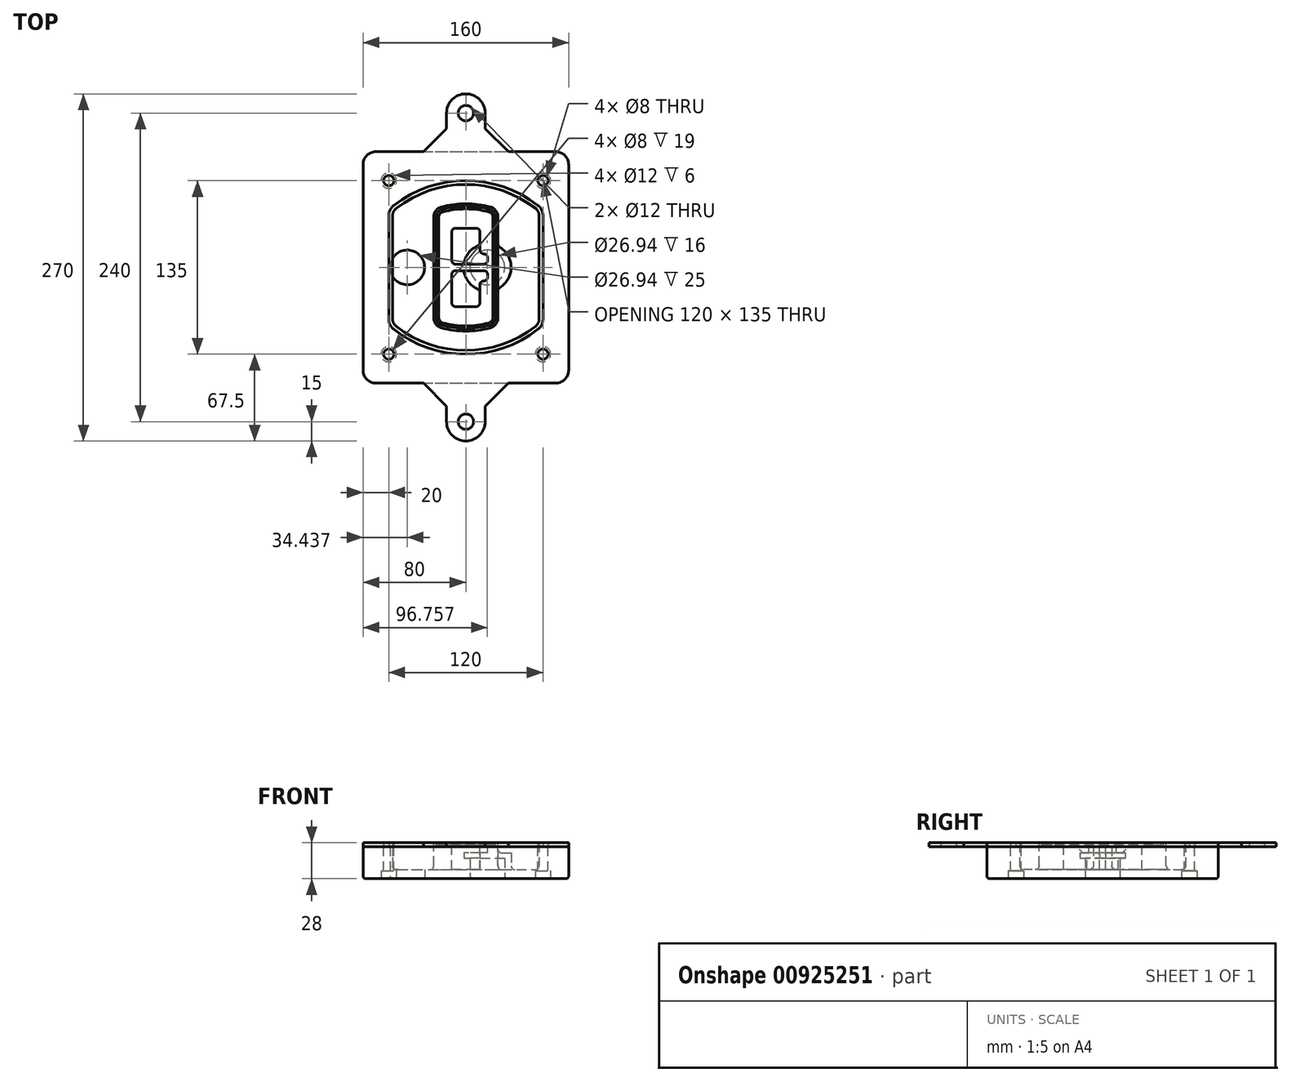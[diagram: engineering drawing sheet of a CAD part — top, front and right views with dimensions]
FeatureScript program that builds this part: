
annotation { "Feature Type Name" : "Feature", "Feature Type Description" : "" }
export const myFeature = defineFeature(function(context is Context, id is Id, definition is map)
    precondition{}
    {
        {
            var Q0;
            Q0=qCreatedBy(makeId("Top.planeOp"),FACE);
            var sketch = newSketch(context, id + "F0", { "sketchPlane" : qUnion([Q0])});
            skPoint(sketch, "E0.rect.middle", {"position": v(0, 0) * mm});
            skLineSegment(sketch, "E1.bottom", {"start": v(-70, -90) * mm, "end": v(70, -90) * mm});
            skLineSegment(sketch, "E1.top", {"start": v(-70, 90) * mm, "end": v(70, 90) * mm});
            skLineSegment(sketch, "E1.left", {"start": v(-80, -80) * mm, "end": v(-80, 80) * mm});
            skLineSegment(sketch, "E1.right", {"start": v(80, -80) * mm, "end": v(80, 80) * mm});
            skLineSegment(sketch, "E2", {"start": v(-80, 90) * mm, "end": v(80, -90) * mm, "construction": true});
            skLineSegment(sketch, "E3", {"start": v(80, 90) * mm, "end": v(-80, -90) * mm, "construction": true});
            skCircle(sketch, "E4", {"center": v(-60, 67.5) * mm, "radius": 4 * mm});
            skCircle(sketch, "E5", {"center": v(60, 67.5) * mm, "radius": 4 * mm});
            skCircle(sketch, "E6", {"center": v(60, -67.5) * mm, "radius": 4 * mm});
            skCircle(sketch, "E7", {"center": v(-60, -67.5) * mm, "radius": 4 * mm});
            skLineSegment(sketch, "E8", {"start": v(-60, 67.5) * mm, "end": v(60, 67.5) * mm, "construction": true});
            skLineSegment(sketch, "E9", {"start": v(60, 67.5) * mm, "end": v(60, -67.5) * mm, "construction": true});
            skLineSegment(sketch, "E10", {"start": v(60, -67.5) * mm, "end": v(-60, -67.5) * mm, "construction": true});
            skLineSegment(sketch, "E11", {"start": v(-60, -67.5) * mm, "end": v(-60, 67.5) * mm, "construction": true});
            skLineSegment(sketch, "E12", {"start": v(-60, 40.3) * mm, "end": v(-60, -40.3) * mm});
            skLineSegment(sketch, "E13", {"start": v(60, 40.3) * mm, "end": v(60, -40.3) * mm});
            skArc(sketch, "E14", {"start": v(56.15, 48.18) * mm, "mid": v(0, 67.5) * mm, "end": v(-56.15, 48.18) * mm});
            skArc(sketch, "E15", {"start": v(-56.15, -48.18) * mm, "mid": v(0, -67.5) * mm, "end": v(56.15, -48.18) * mm});
            skLineSegment(sketch, "E16", {"start": v(-60, 0) * mm, "end": v(60, 0) * mm, "construction": true});
            skPoint(sketch, "E17.visualSharp", {"position": v(-60, -45) * mm});
            skArc(sketch, "E17.filletArc", {"start": v(-60, -40.3) * mm, "mid": v(-58.99, -44.68) * mm, "end": v(-56.15, -48.18) * mm});
            skPoint(sketch, "E18.visualSharp", {"position": v(-60, 45) * mm});
            skArc(sketch, "E18.filletArc", {"start": v(-56.15, 48.18) * mm, "mid": v(-58.99, 44.68) * mm, "end": v(-60, 40.3) * mm});
            skPoint(sketch, "E19.visualSharp", {"position": v(60, 45) * mm});
            skArc(sketch, "E19.filletArc", {"start": v(60, 40.3) * mm, "mid": v(58.99, 44.68) * mm, "end": v(56.15, 48.18) * mm});
            skPoint(sketch, "E20.visualSharp", {"position": v(60, -45) * mm});
            skArc(sketch, "E20.filletArc", {"start": v(56.15, -48.18) * mm, "mid": v(58.99, -44.68) * mm, "end": v(60, -40.3) * mm});
            skPoint(sketch, "E21.visualSharp", {"position": v(-80, 90) * mm});
            skArc(sketch, "E21.filletArc", {"start": v(-70, 90) * mm, "mid": v(-77.07, 87.07) * mm, "end": v(-80, 80) * mm});
            skPoint(sketch, "E22.visualSharp", {"position": v(80, 90) * mm});
            skArc(sketch, "E22.filletArc", {"start": v(80, 80) * mm, "mid": v(77.07, 87.07) * mm, "end": v(70, 90) * mm});
            skPoint(sketch, "E23.visualSharp", {"position": v(80, -90) * mm});
            skArc(sketch, "E23.filletArc", {"start": v(70, -90) * mm, "mid": v(77.07, -87.07) * mm, "end": v(80, -80) * mm});
            skPoint(sketch, "E24.visualSharp", {"position": v(-80, -90) * mm});
            skArc(sketch, "E24.filletArc", {"start": v(-80, -80) * mm, "mid": v(-77.07, -87.07) * mm, "end": v(-70, -90) * mm});
            skArc(sketch, "E25.0", {"start": v(57, 40.3) * mm, "mid": v(56.3, 43.36) * mm, "end": v(54.3, 45.81) * mm});
            skLineSegment(sketch, "E25.1", {"start": v(57, 40.3) * mm, "end": v(57, -40.3) * mm});
            skArc(sketch, "E25.2", {"start": v(54.3, -45.81) * mm, "mid": v(56.3, -43.36) * mm, "end": v(57, -40.3) * mm});
            skArc(sketch, "E25.3", {"start": v(-54.3, -45.81) * mm, "mid": v(0, -64.5) * mm, "end": v(54.3, -45.81) * mm});
            skArc(sketch, "E25.4", {"start": v(-57, -40.3) * mm, "mid": v(-56.3, -43.36) * mm, "end": v(-54.3, -45.81) * mm});
            skArc(sketch, "E25.5", {"start": v(54.3, 45.81) * mm, "mid": v(0, 64.5) * mm, "end": v(-54.3, 45.81) * mm});
            skLineSegment(sketch, "E25.6", {"start": v(-57, 40.3) * mm, "end": v(-57, -40.3) * mm});
            skArc(sketch, "E25.7", {"start": v(-54.3, 45.81) * mm, "mid": v(-56.3, 43.36) * mm, "end": v(-57, 40.3) * mm});
            skArc(sketch, "E26.0", {"start": v(-58.62, 51.33) * mm, "mid": v(-62.58, 46.43) * mm, "end": v(-64, 40.3) * mm});
            skArc(sketch, "E26.1", {"start": v(58.62, 51.33) * mm, "mid": v(0, 71.5) * mm, "end": v(-58.62, 51.33) * mm});
            skArc(sketch, "E26.2", {"start": v(64, 40.3) * mm, "mid": v(62.58, 46.43) * mm, "end": v(58.62, 51.33) * mm});
            skLineSegment(sketch, "E26.3", {"start": v(64, 40.3) * mm, "end": v(64, -40.3) * mm});
            skArc(sketch, "E26.4", {"start": v(58.62, -51.33) * mm, "mid": v(62.58, -46.43) * mm, "end": v(64, -40.3) * mm});
            skLineSegment(sketch, "E26.5", {"start": v(-64, 40.3) * mm, "end": v(-64, -40.3) * mm});
            skArc(sketch, "E26.6", {"start": v(-58.62, -51.33) * mm, "mid": v(0, -71.5) * mm, "end": v(58.62, -51.33) * mm});
            skArc(sketch, "E26.7", {"start": v(-64, -40.3) * mm, "mid": v(-62.58, -46.43) * mm, "end": v(-58.62, -51.33) * mm});
            skSolve(sketch);
        }
        {
            var Q0;
            Q0=makeQuery(id+"F0.imprint","IMPRINT",FACE,{"disambiguationData":[TD([[makeQuery(id+"F0.imprint","IMPRINT",EDGE,{"derivedFrom":sQuery(id+"F0.wireOp",EDGE,"E1.bottom")}),1.0]])]});
            var Q1;
            Q1=makeQuery(id+"F0.imprint","IMPRINT",FACE,{"disambiguationData":[TD([[makeQuery(id+"F0.imprint","IMPRINT",EDGE,{"derivedFrom":sQuery(id+"F0.wireOp",EDGE,"E12")}),1.0]])]});
            var Q2;
            Q2=makeQuery(id+"F0.imprint","IMPRINT",FACE,{"disambiguationData":[TD([[makeQuery(id+"F0.imprint","IMPRINT",EDGE,{"derivedFrom":sQuery(id+"F0.wireOp",EDGE,"E25.0")}),1.0]])]});
            var Q3;
            Q3=makeQuery(id+"F0.imprint","IMPRINT",FACE,{"disambiguationData":[TD([[makeQuery(id+"F0.imprint","IMPRINT",EDGE,{"derivedFrom":sQuery(id+"F0.wireOp",EDGE,"E12")}),-1.0]])]});
            extrude(context, id + "F1", {"entities" : qUnion([Q0, Q1, Q2, Q3]), "oppositeDirection" : true, "depth" : 25 * mm});
        }
        {
            var Q0;
            Q0=makeQuery(id+"F0.imprint","IMPRINT",FACE,{"disambiguationData":[TD([[makeQuery(id+"F0.imprint","IMPRINT",EDGE,{"derivedFrom":sQuery(id+"F0.wireOp",EDGE,"E12")}),1.0]])]});
            extrude(context, id + "F2", {"entities" : qUnion([Q0]), "operationType" : NewBodyOperationType.ADD, "depth" : 3 * mm});
        }
        {
            var Q0;
            Q0=makeQuery(id+"F0.imprint","IMPRINT",FACE,{"disambiguationData":[TD([[makeQuery(id+"F0.imprint","IMPRINT",EDGE,{"derivedFrom":sQuery(id+"F0.wireOp",EDGE,"E25.0")}),1.0]])]});
            extrude(context, id + "F3", {"entities" : qUnion([Q0]), "operationType" : NewBodyOperationType.REMOVE, "oppositeDirection" : true, "depth" : 18 * mm});
        }
        {
            var Q0;
            Q0=makeQuery(id+"F2.opExtrude","CAP_FACE",FACE,{"disambiguationData":[OSD([sQuery(id+"F0.wireOp",EDGE,"E12"),sQuery(id+"F0.wireOp",EDGE,"E13"),sQuery(id+"F0.wireOp",EDGE,"E14"),sQuery(id+"F0.wireOp",EDGE,"E15"),sQuery(id+"F0.wireOp",EDGE,"E17.filletArc"),sQuery(id+"F0.wireOp",EDGE,"E18.filletArc"),sQuery(id+"F0.wireOp",EDGE,"E19.filletArc"),sQuery(id+"F0.wireOp",EDGE,"E20.filletArc"),sQuery(id+"F0.wireOp",EDGE,"E25.0"),sQuery(id+"F0.wireOp",EDGE,"E25.1"),sQuery(id+"F0.wireOp",EDGE,"E25.2"),sQuery(id+"F0.wireOp",EDGE,"E25.3"),sQuery(id+"F0.wireOp",EDGE,"E25.4"),sQuery(id+"F0.wireOp",EDGE,"E25.5"),sQuery(id+"F0.wireOp",EDGE,"E25.6"),sQuery(id+"F0.wireOp",EDGE,"E25.7")])],"isStart":false});
            var sketch = newSketch(context, id + "F4", { "sketchPlane" : qUnion([Q0])});
            skArc(sketch, "E27.0", {"start": v(-19.08, -46.97) * mm, "mid": v(0, -49.5) * mm, "end": v(19.08, -46.97) * mm});
            skArc(sketch, "E28.0", {"start": v(19.08, 46.97) * mm, "mid": v(0, 49.5) * mm, "end": v(-19.08, 46.97) * mm});
            skLineSegment(sketch, "E29", {"start": v(-25, 39.25) * mm, "end": v(-25, -39.25) * mm});
            skLineSegment(sketch, "E30", {"start": v(25, 39.25) * mm, "end": v(25, -39.25) * mm});
            skLineSegment(sketch, "E31", {"start": v(-25, 45.1) * mm, "end": v(25, 45.1) * mm, "construction": true});
            skLineSegment(sketch, "E32", {"start": v(-25, -45.1) * mm, "end": v(25, -45.1) * mm, "construction": true});
            skPoint(sketch, "E33.visualSharp", {"position": v(-25, 45.1) * mm});
            skArc(sketch, "E33.filletArc", {"start": v(-19.08, 46.97) * mm, "mid": v(-23.35, 44.11) * mm, "end": v(-25, 39.25) * mm});
            skPoint(sketch, "E34.visualSharp", {"position": v(25, 45.1) * mm});
            skArc(sketch, "E34.filletArc", {"start": v(25, 39.25) * mm, "mid": v(23.35, 44.11) * mm, "end": v(19.08, 46.97) * mm});
            skPoint(sketch, "E35.visualSharp", {"position": v(25, -45.1) * mm});
            skArc(sketch, "E35.filletArc", {"start": v(19.08, -46.97) * mm, "mid": v(23.35, -44.11) * mm, "end": v(25, -39.25) * mm});
            skPoint(sketch, "E36.visualSharp", {"position": v(-25, -45.1) * mm});
            skArc(sketch, "E36.filletArc", {"start": v(-25, -39.25) * mm, "mid": v(-23.35, -44.11) * mm, "end": v(-19.08, -46.97) * mm});
            skArc(sketch, "E37.0", {"start": v(54.3, 45.81) * mm, "mid": v(0, 64.5) * mm, "end": v(-54.3, 45.81) * mm});
            skArc(sketch, "E37.1", {"start": v(-54.3, 45.81) * mm, "mid": v(-56.3, 43.36) * mm, "end": v(-57, 40.3) * mm});
            skLineSegment(sketch, "E37.2", {"start": v(-57, 40.3) * mm, "end": v(-57, -40.3) * mm});
            skArc(sketch, "E37.3", {"start": v(-57, -40.3) * mm, "mid": v(-56.3, -43.36) * mm, "end": v(-54.3, -45.81) * mm});
            skArc(sketch, "E37.4", {"start": v(-54.3, -45.81) * mm, "mid": v(0, -64.5) * mm, "end": v(54.3, -45.81) * mm});
            skArc(sketch, "E37.5", {"start": v(54.3, -45.81) * mm, "mid": v(56.3, -43.36) * mm, "end": v(57, -40.3) * mm});
            skLineSegment(sketch, "E37.6", {"start": v(57, 40.3) * mm, "end": v(57, -40.3) * mm});
            skArc(sketch, "E37.7", {"start": v(57, 40.3) * mm, "mid": v(56.3, 43.36) * mm, "end": v(54.3, 45.81) * mm});
            skLineSegment(sketch, "E38.0", {"start": v(23, 39.25) * mm, "end": v(23, -39.25) * mm});
            skArc(sketch, "E38.1", {"start": v(18.56, -45.04) * mm, "mid": v(21.76, -42.9) * mm, "end": v(23, -39.25) * mm});
            skArc(sketch, "E38.2", {"start": v(-18.56, -45.04) * mm, "mid": v(0, -47.5) * mm, "end": v(18.56, -45.04) * mm});
            skArc(sketch, "E38.3", {"start": v(-23, -39.25) * mm, "mid": v(-21.76, -42.9) * mm, "end": v(-18.56, -45.04) * mm});
            skLineSegment(sketch, "E38.4", {"start": v(-23, 39.25) * mm, "end": v(-23, -39.25) * mm});
            skArc(sketch, "E38.5", {"start": v(23, 39.25) * mm, "mid": v(21.76, 42.9) * mm, "end": v(18.56, 45.04) * mm});
            skArc(sketch, "E38.6", {"start": v(-18.56, 45.04) * mm, "mid": v(-21.76, 42.9) * mm, "end": v(-23, 39.25) * mm});
            skArc(sketch, "E38.7", {"start": v(18.56, 45.04) * mm, "mid": v(0, 47.5) * mm, "end": v(-18.56, 45.04) * mm});
            skArc(sketch, "E39.0", {"start": v(21, 39.25) * mm, "mid": v(20.18, 41.68) * mm, "end": v(18.04, 43.1) * mm});
            skLineSegment(sketch, "E39.1", {"start": v(21, 39.25) * mm, "end": v(21, -39.25) * mm});
            skArc(sketch, "E39.2", {"start": v(18.04, -43.1) * mm, "mid": v(20.18, -41.68) * mm, "end": v(21, -39.25) * mm});
            skArc(sketch, "E39.3", {"start": v(-18.04, -43.1) * mm, "mid": v(0, -45.5) * mm, "end": v(18.04, -43.1) * mm});
            skArc(sketch, "E39.4", {"start": v(-21, -39.25) * mm, "mid": v(-20.18, -41.68) * mm, "end": v(-18.04, -43.1) * mm});
            skArc(sketch, "E39.5", {"start": v(18.04, 43.1) * mm, "mid": v(0, 45.5) * mm, "end": v(-18.04, 43.1) * mm});
            skLineSegment(sketch, "E39.6", {"start": v(-21, 39.25) * mm, "end": v(-21, -39.25) * mm});
            skArc(sketch, "E39.7", {"start": v(-18.04, 43.1) * mm, "mid": v(-20.18, 41.68) * mm, "end": v(-21, 39.25) * mm});
            skLineSegment(sketch, "E40", {"start": v(-25, 0) * mm, "end": v(25, 0) * mm, "construction": true});
            skLineSegment(sketch, "E41", {"start": v(-11, 5.5) * mm, "end": v(-11, 27.5) * mm});
            skLineSegment(sketch, "E42", {"start": v(-8, 30.5) * mm, "end": v(8, 30.5) * mm});
            skLineSegment(sketch, "E43", {"start": v(11, 27.5) * mm, "end": v(11, 13.5) * mm});
            skLineSegment(sketch, "E44", {"start": v(14, 10.5) * mm, "end": v(14, 10.5) * mm});
            skLineSegment(sketch, "E45", {"start": v(17, 7.5) * mm, "end": v(17, 5.5) * mm});
            skLineSegment(sketch, "E46", {"start": v(14, 2.5) * mm, "end": v(-8, 2.5) * mm});
            skPoint(sketch, "E47.visualSharp", {"position": v(-11, 30.5) * mm});
            skArc(sketch, "E47.filletArc", {"start": v(-8, 30.5) * mm, "mid": v(-10.12, 29.62) * mm, "end": v(-11, 27.5) * mm});
            skPoint(sketch, "E48.visualSharp", {"position": v(11, 30.5) * mm});
            skArc(sketch, "E48.filletArc", {"start": v(11, 27.5) * mm, "mid": v(10.12, 29.62) * mm, "end": v(8, 30.5) * mm});
            skPoint(sketch, "E49.visualSharp", {"position": v(11, 10.5) * mm});
            skArc(sketch, "E49.filletArc", {"start": v(11, 13.5) * mm, "mid": v(11.88, 11.38) * mm, "end": v(14, 10.5) * mm});
            skPoint(sketch, "E50.visualSharp", {"position": v(17, 10.5) * mm});
            skArc(sketch, "E50.filletArc", {"start": v(17, 7.5) * mm, "mid": v(16.12, 9.62) * mm, "end": v(14, 10.5) * mm});
            skPoint(sketch, "E51.visualSharp", {"position": v(17, 2.5) * mm});
            skArc(sketch, "E51.filletArc", {"start": v(14, 2.5) * mm, "mid": v(16.12, 3.38) * mm, "end": v(17, 5.5) * mm});
            skPoint(sketch, "E52.visualSharp", {"position": v(-11, 2.5) * mm});
            skArc(sketch, "E52.filletArc", {"start": v(-11, 5.5) * mm, "mid": v(-10.12, 3.38) * mm, "end": v(-8, 2.5) * mm});
            skLineSegment(sketch, "E53.0.MirrorCS", {"start": v(14, -2.5) * mm, "end": v(-8, -2.5) * mm});
            skArc(sketch, "E54.0.MirrorCS", {"start": v(-11, -5.5) * mm, "mid": v(-10.12, -3.38) * mm, "end": v(-8, -2.5) * mm});
            skLineSegment(sketch, "E55.0.MirrorCS", {"start": v(-11, -5.5) * mm, "end": v(-11, -27.5) * mm});
            skArc(sketch, "E56.0.MirrorCS", {"start": v(-8, -30.5) * mm, "mid": v(-10.12, -29.62) * mm, "end": v(-11, -27.5) * mm});
            skLineSegment(sketch, "E57.0.MirrorCS", {"start": v(-8, -30.5) * mm, "end": v(8, -30.5) * mm});
            skArc(sketch, "E58.0.MirrorCS", {"start": v(11, -27.5) * mm, "mid": v(10.12, -29.62) * mm, "end": v(8, -30.5) * mm});
            skLineSegment(sketch, "E59.0.MirrorCS", {"start": v(11, -27.5) * mm, "end": v(11, -13.5) * mm});
            skArc(sketch, "E60.0.MirrorCS", {"start": v(11, -13.5) * mm, "mid": v(11.88, -11.38) * mm, "end": v(14, -10.5) * mm});
            skArc(sketch, "E61.0.MirrorCS", {"start": v(17, -7.5) * mm, "mid": v(16.12, -9.62) * mm, "end": v(14, -10.5) * mm});
            skLineSegment(sketch, "E62.0.MirrorCS", {"start": v(17, -7.5) * mm, "end": v(17, -5.5) * mm});
            skArc(sketch, "E63.0.MirrorCS", {"start": v(14, -2.5) * mm, "mid": v(16.12, -3.38) * mm, "end": v(17, -5.5) * mm});
            skSolve(sketch);
        }
        {
            var Q0;
            Q0=makeQuery(id+"F4.imprint","IMPRINT",FACE,{"disambiguationData":[TD([[makeQuery(id+"F4.imprint","IMPRINT",EDGE,{"derivedFrom":sQuery(id+"F4.wireOp",EDGE,"E27.0")}),1.0]])]});
            var Q1;
            Q1=makeQuery(id+"F4.imprint","IMPRINT",FACE,{"disambiguationData":[TD([[makeQuery(id+"F4.imprint","IMPRINT",EDGE,{"derivedFrom":sQuery(id+"F4.wireOp",EDGE,"E38.0")}),-1.0]])]});
            var Q2;
            Q2=makeQuery(id+"F4.imprint","IMPRINT",FACE,{"disambiguationData":[TD([[makeQuery(id+"F4.imprint","IMPRINT",EDGE,{"derivedFrom":sQuery(id+"F4.wireOp",EDGE,"E39.0")}),1.0]])]});
            extrude(context, id + "F5", {"entities" : qUnion([Q0, Q1, Q2]), "operationType" : NewBodyOperationType.ADD, "endBound" : BoundingType.UP_TO_NEXT, "oppositeDirection" : true, "depth" : 25 * mm});
        }
        {
            var Q0;
            Q0=makeQuery(id+"F4.imprint","IMPRINT",FACE,{"disambiguationData":[TD([[makeQuery(id+"F4.imprint","IMPRINT",EDGE,{"derivedFrom":sQuery(id+"F4.wireOp",EDGE,"E38.0")}),-1.0]])]});
            extrude(context, id + "F6", {"entities" : qUnion([Q0]), "operationType" : NewBodyOperationType.REMOVE, "oppositeDirection" : true, "depth" : 2 * mm});
        }
        {
            var Q0;
            Q0=makeQuery(id+"F1.opExtrude","CAP_FACE",FACE,{"disambiguationData":[OSD([sQuery(id+"F0.wireOp",EDGE,"E1.bottom"),sQuery(id+"F0.wireOp",EDGE,"E1.top"),sQuery(id+"F0.wireOp",EDGE,"E1.left"),sQuery(id+"F0.wireOp",EDGE,"E1.right"),sQuery(id+"F0.wireOp",EDGE,"E4"),sQuery(id+"F0.wireOp",EDGE,"E5"),sQuery(id+"F0.wireOp",EDGE,"E6"),sQuery(id+"F0.wireOp",EDGE,"E7"),sQuery(id+"F0.wireOp",EDGE,"E21.filletArc"),sQuery(id+"F0.wireOp",EDGE,"E22.filletArc"),sQuery(id+"F0.wireOp",EDGE,"E23.filletArc"),sQuery(id+"F0.wireOp",EDGE,"E24.filletArc")])],"isStart":false});
            var sketch = newSketch(context, id + "F7", { "sketchPlane" : qUnion([Q0])});
            skCircle(sketch, "E64", {"center": v(16.76, 0) * mm, "radius": 13.47 * mm});
            skCircle(sketch, "E65", {"center": v(-45.56, 0) * mm, "radius": 13.47 * mm});
            skLineSegment(sketch, "E66", {"start": v(80, 0) * mm, "end": v(-80, 0) * mm});
            skCircle(sketch, "E67", {"center": v(16.76, 0) * mm, "radius": 18.47 * mm});
            skCircle(sketch, "E68", {"center": v(60, -67.5) * mm, "radius": 6 * mm});
            skCircle(sketch, "E69", {"center": v(-60, -67.5) * mm, "radius": 6 * mm});
            skCircle(sketch, "E70", {"center": v(-60, 67.5) * mm, "radius": 6 * mm});
            skCircle(sketch, "E71", {"center": v(60, 67.5) * mm, "radius": 6 * mm});
            skSolve(sketch);
        }
        {
            var Q0;
            {var subQ1=sQuery(id+"F7.wireOp",EDGE,"E66");var subQ4=sQuery(id+"F7.wireOp",EDGE,"E64");var subQ6=makeQuery(id+"F7.imprint","INTERSECT",VERTEX,{"disambiguationData":[OD(0.0)],"derivedFrom":[subQ4,subQ1]});Q0=makeQuery(id+"F7.imprint","IMPRINT",FACE,{"disambiguationData":[TD([[makeQuery(id+"F7.imprint","IMPRINT",EDGE,{"disambiguationData":[TD([[subQ6,-1.0]])],"derivedFrom":subQ4}),-1.0]])]});}
            var Q1;
            {var subQ0=sQuery(id+"F7.wireOp",EDGE,"E66");var subQ1=sQuery(id+"F7.wireOp",EDGE,"E64");var subQ3=makeQuery(id+"F7.imprint","INTERSECT",VERTEX,{"disambiguationData":[OD(0.0)],"derivedFrom":[subQ1,subQ0]});Q1=makeQuery(id+"F7.imprint","IMPRINT",FACE,{"disambiguationData":[TD([[makeQuery(id+"F7.imprint","IMPRINT",EDGE,{"disambiguationData":[TD([[subQ3,-1.0]])],"derivedFrom":subQ1}),1.0]])]});}
            var Q2;
            {var subQ0=sQuery(id+"F7.wireOp",EDGE,"E66");var subQ1=sQuery(id+"F7.wireOp",EDGE,"E64");var subQ3=makeQuery(id+"F7.imprint","INTERSECT",VERTEX,{"disambiguationData":[OD(0.0)],"derivedFrom":[subQ1,subQ0]});Q2=makeQuery(id+"F7.imprint","IMPRINT",FACE,{"disambiguationData":[TD([[makeQuery(id+"F7.imprint","IMPRINT",EDGE,{"disambiguationData":[TD([[subQ3,1.0]])],"derivedFrom":subQ1}),1.0]])]});}
            var Q3;
            {var subQ1=sQuery(id+"F7.wireOp",EDGE,"E66");var subQ4=sQuery(id+"F7.wireOp",EDGE,"E64");var subQ6=makeQuery(id+"F7.imprint","INTERSECT",VERTEX,{"disambiguationData":[OD(0.0)],"derivedFrom":[subQ4,subQ1]});Q3=makeQuery(id+"F7.imprint","IMPRINT",FACE,{"disambiguationData":[TD([[makeQuery(id+"F7.imprint","IMPRINT",EDGE,{"disambiguationData":[TD([[subQ6,1.0]])],"derivedFrom":subQ4}),-1.0]])]});}
            extrude(context, id + "F8", {"entities" : qUnion([Q0, Q1, Q2, Q3]), "operationType" : NewBodyOperationType.ADD, "oppositeDirection" : true, "depth" : 20 * mm});
        }
        {
            var Q0;
            {var subQ0=sQuery(id+"F7.wireOp",EDGE,"E66");var subQ1=sQuery(id+"F7.wireOp",EDGE,"E64");var subQ3=makeQuery(id+"F7.imprint","INTERSECT",VERTEX,{"disambiguationData":[OD(0.0)],"derivedFrom":[subQ1,subQ0]});Q0=makeQuery(id+"F7.imprint","IMPRINT",FACE,{"disambiguationData":[TD([[makeQuery(id+"F7.imprint","IMPRINT",EDGE,{"disambiguationData":[TD([[subQ3,-1.0]])],"derivedFrom":subQ1}),1.0]])]});}
            var Q1;
            {var subQ0=sQuery(id+"F7.wireOp",EDGE,"E66");var subQ1=sQuery(id+"F7.wireOp",EDGE,"E64");var subQ3=makeQuery(id+"F7.imprint","INTERSECT",VERTEX,{"disambiguationData":[OD(0.0)],"derivedFrom":[subQ1,subQ0]});Q1=makeQuery(id+"F7.imprint","IMPRINT",FACE,{"disambiguationData":[TD([[makeQuery(id+"F7.imprint","IMPRINT",EDGE,{"disambiguationData":[TD([[subQ3,1.0]])],"derivedFrom":subQ1}),1.0]])]});}
            extrude(context, id + "F9", {"entities" : qUnion([Q0, Q1]), "operationType" : NewBodyOperationType.REMOVE, "oppositeDirection" : true, "depth" : 16 * mm});
        }
        {
            var Q0;
            {var subQ0=sQuery(id+"F7.wireOp",EDGE,"E66");var subQ1=sQuery(id+"F7.wireOp",EDGE,"E65");var subQ3=makeQuery(id+"F7.imprint","INTERSECT",VERTEX,{"disambiguationData":[OD(0.0)],"derivedFrom":[subQ1,subQ0]});Q0=makeQuery(id+"F7.imprint","IMPRINT",FACE,{"disambiguationData":[TD([[makeQuery(id+"F7.imprint","IMPRINT",EDGE,{"disambiguationData":[TD([[subQ3,-1.0]])],"derivedFrom":subQ1}),1.0]])]});}
            var Q1;
            {var subQ0=sQuery(id+"F7.wireOp",EDGE,"E66");var subQ1=sQuery(id+"F7.wireOp",EDGE,"E65");var subQ3=makeQuery(id+"F7.imprint","INTERSECT",VERTEX,{"disambiguationData":[OD(0.0)],"derivedFrom":[subQ1,subQ0]});Q1=makeQuery(id+"F7.imprint","IMPRINT",FACE,{"disambiguationData":[TD([[makeQuery(id+"F7.imprint","IMPRINT",EDGE,{"disambiguationData":[TD([[subQ3,1.0]])],"derivedFrom":subQ1}),1.0]])]});}
            extrude(context, id + "F10", {"entities" : qUnion([Q0, Q1]), "operationType" : NewBodyOperationType.REMOVE, "oppositeDirection" : true, "depth" : 25 * mm});
        }
        {
            var Q0;
            Q0=makeQuery(id+"F7.imprint","IMPRINT",FACE,{"disambiguationData":[TD([[makeQuery(id+"F7.imprint","IMPRINT",EDGE,{"derivedFrom":sQuery(id+"F7.wireOp",EDGE,"E68")}),1.0]])]});
            var Q1;
            Q1=makeQuery(id+"F7.imprint","IMPRINT",FACE,{"disambiguationData":[TD([[makeQuery(id+"F7.imprint","IMPRINT",EDGE,{"derivedFrom":makeQuery(id+"F1.opExtrude","CAP_EDGE",EDGE,{"disambiguationData":[OSD([sQuery(id+"F0.wireOp",EDGE,"E5")])],"isStart":false})}),-1.0]])]});
            var Q2;
            Q2=makeQuery(id+"F7.imprint","IMPRINT",FACE,{"disambiguationData":[TD([[makeQuery(id+"F7.imprint","IMPRINT",EDGE,{"derivedFrom":sQuery(id+"F7.wireOp",EDGE,"E69")}),1.0]])]});
            var Q3;
            Q3=makeQuery(id+"F7.imprint","IMPRINT",FACE,{"disambiguationData":[TD([[makeQuery(id+"F7.imprint","IMPRINT",EDGE,{"derivedFrom":makeQuery(id+"F1.opExtrude","CAP_EDGE",EDGE,{"disambiguationData":[OSD([sQuery(id+"F0.wireOp",EDGE,"E4")])],"isStart":false})}),-1.0]])]});
            var Q4;
            Q4=makeQuery(id+"F7.imprint","IMPRINT",FACE,{"disambiguationData":[TD([[makeQuery(id+"F7.imprint","IMPRINT",EDGE,{"derivedFrom":sQuery(id+"F7.wireOp",EDGE,"E70")}),1.0]])]});
            var Q5;
            Q5=makeQuery(id+"F7.imprint","IMPRINT",FACE,{"disambiguationData":[TD([[makeQuery(id+"F7.imprint","IMPRINT",EDGE,{"derivedFrom":makeQuery(id+"F1.opExtrude","CAP_EDGE",EDGE,{"disambiguationData":[OSD([sQuery(id+"F0.wireOp",EDGE,"E7")])],"isStart":false})}),-1.0]])]});
            var Q6;
            Q6=makeQuery(id+"F7.imprint","IMPRINT",FACE,{"disambiguationData":[TD([[makeQuery(id+"F7.imprint","IMPRINT",EDGE,{"derivedFrom":sQuery(id+"F7.wireOp",EDGE,"E71")}),1.0]])]});
            var Q7;
            Q7=makeQuery(id+"F7.imprint","IMPRINT",FACE,{"disambiguationData":[TD([[makeQuery(id+"F7.imprint","IMPRINT",EDGE,{"derivedFrom":makeQuery(id+"F1.opExtrude","CAP_EDGE",EDGE,{"disambiguationData":[OSD([sQuery(id+"F0.wireOp",EDGE,"E6")])],"isStart":false})}),-1.0]])]});
            extrude(context, id + "F11", {"entities" : qUnion([Q0, Q1, Q2, Q3, Q4, Q5, Q6, Q7]), "operationType" : NewBodyOperationType.REMOVE, "oppositeDirection" : true, "depth" : 6 * mm});
        }
        {
            var Q0;
            Q0=makeQuery(id+"F9.boolean.opBoolean","COPY",FACE,{"derivedFrom":makeQuery(id+"F9.opExtrude","CAP_FACE",FACE,{"disambiguationData":[OSD([sQuery(id+"F7.wireOp",EDGE,"E64")])],"isStart":false})});
            var sketch = newSketch(context, id + "F12", { "sketchPlane" : qUnion([Q0])});
            skArc(sketch, "E72.0", {"start": v(11, 17.55) * mm, "mid": v(2.57, 11.82) * mm, "end": v(-1.54, 2.5) * mm});
            skArc(sketch, "E72.1", {"start": v(-1.54, -2.5) * mm, "mid": v(2.57, -11.82) * mm, "end": v(11, -17.55) * mm});
            skLineSegment(sketch, "E73", {"start": v(-1.54, -2.5) * mm, "end": v(14, -2.5) * mm});
            skLineSegment(sketch, "E74.0", {"start": v(14, 2.5) * mm, "end": v(-1.54, 2.5) * mm});
            skArc(sketch, "E74.1", {"start": v(14, 2.5) * mm, "mid": v(16.12, 3.38) * mm, "end": v(17, 5.5) * mm});
            skLineSegment(sketch, "E74.2", {"start": v(17, 7.5) * mm, "end": v(17, 5.5) * mm});
            skArc(sketch, "E74.3", {"start": v(17, 7.5) * mm, "mid": v(16.12, 9.62) * mm, "end": v(14, 10.5) * mm});
            skArc(sketch, "E74.4", {"start": v(11, 13.5) * mm, "mid": v(11.88, 11.38) * mm, "end": v(14, 10.5) * mm});
            skLineSegment(sketch, "E74.5", {"start": v(11, 17.55) * mm, "end": v(11, 13.5) * mm});
            skLineSegment(sketch, "E74.7", {"start": v(14, -2.5) * mm, "end": v(-1.54, -2.5) * mm});
            skArc(sketch, "E74.8", {"start": v(14, -2.5) * mm, "mid": v(16.12, -3.38) * mm, "end": v(17, -5.5) * mm});
            skLineSegment(sketch, "E74.9", {"start": v(17, -7.5) * mm, "end": v(17, -5.5) * mm});
            skArc(sketch, "E74.10", {"start": v(17, -7.5) * mm, "mid": v(16.12, -9.62) * mm, "end": v(14, -10.5) * mm});
            skArc(sketch, "E74.11", {"start": v(11, -13.5) * mm, "mid": v(11.88, -11.38) * mm, "end": v(14, -10.5) * mm});
            skLineSegment(sketch, "E74.12", {"start": v(11, -17.55) * mm, "end": v(11, -13.5) * mm});
            skPoint(sketch, "E75.orphan", {"position": v(11, -27.5) * mm});
            skPoint(sketch, "E76.orphan", {"position": v(-8, -2.5) * mm});
            skPoint(sketch, "E77.orphan", {"position": v(-8, 2.5) * mm});
            skPoint(sketch, "E78.orphan", {"position": v(11, 27.5) * mm});
            skSolve(sketch);
        }
        {
            var Q0;
            {var subQ7=sQuery(id+"F12.wireOp",EDGE,"E72.0");var subQ14=sQuery(id+"F12.wireOp",EDGE,"E72.1");var subQ16=sQuery(id+"F12.wireOp",EDGE,"E74.1");var subQ18=sQuery(id+"F12.wireOp",EDGE,"E74.8");Q0=qUnion([makeQuery(id+"F12.imprint","IMPRINT",FACE,{"disambiguationData":[TD([[makeQuery(id+"F12.imprint","IMPRINT",EDGE,{"derivedFrom":subQ7}),1.0]])]}),makeQuery(id+"F12.imprint","IMPRINT",FACE,{"disambiguationData":[TD([[makeQuery(id+"F12.imprint","IMPRINT",EDGE,{"derivedFrom":subQ14}),1.0]])]}),makeQuery(id+"F12.imprint","IMPRINT",FACE,{"disambiguationData":[TD([[makeQuery(id+"F12.imprint","IMPRINT",EDGE,{"derivedFrom":subQ16}),1.0]])]}),makeQuery(id+"F12.imprint","IMPRINT",FACE,{"disambiguationData":[TD([[makeQuery(id+"F12.imprint","IMPRINT",EDGE,{"derivedFrom":subQ18}),-1.0]])]})]);}
            var Q1;
            Q1=makeQuery(id+"F5.boolean.opBoolean","SPLIT",FACE,{"disambiguationData":[TD([makeQuery(id+"F5.opExtrude","SWEPT_FACE",FACE,{"disambiguationData":[OSD([sQuery(id+"F4.wireOp",EDGE,"E41")])]})])],"derivedFrom":makeQuery(id+"F3.boolean.opBoolean","COPY",FACE,{"derivedFrom":makeQuery(id+"F3.opExtrude","CAP_FACE",FACE,{"disambiguationData":[OSD([sQuery(id+"F0.wireOp",EDGE,"E25.0"),sQuery(id+"F0.wireOp",EDGE,"E25.1"),sQuery(id+"F0.wireOp",EDGE,"E25.2"),sQuery(id+"F0.wireOp",EDGE,"E25.3"),sQuery(id+"F0.wireOp",EDGE,"E25.4"),sQuery(id+"F0.wireOp",EDGE,"E25.5"),sQuery(id+"F0.wireOp",EDGE,"E25.6"),sQuery(id+"F0.wireOp",EDGE,"E25.7")])],"isStart":false})})});
            extrude(context, id + "F13", {"entities" : qUnion([Q0]), "operationType" : NewBodyOperationType.REMOVE, "endBound" : BoundingType.UP_TO_SURFACE, "endBoundEntityFace" : qUnion([Q1]), "depth" : 25 * mm});
        }
        {
            var Q0;
            Q0=makeQuery(id+"F3.boolean.opBoolean","COPY",EDGE,{"derivedFrom":makeQuery(id+"F3.opExtrude","CAP_EDGE",EDGE,{"disambiguationData":[OSD([sQuery(id+"F0.wireOp",EDGE,"E25.6")])],"isStart":false})});
            var Q1;
            Q1=makeQuery(id+"F8.boolean.opBoolean","INTERSECT",EDGE,{"derivedFrom":[makeQuery(id+"F5.opExtrude","SWEPT_FACE",FACE,{"disambiguationData":[OSD([sQuery(id+"F4.wireOp",EDGE,"E30")])]}),makeQuery(id+"F8.opExtrude","CAP_FACE",FACE,{"disambiguationData":[OSD([sQuery(id+"F7.wireOp",EDGE,"E67")])],"isStart":false})]});
            var Q2;
            Q2=makeQuery(id+"F8.boolean.opBoolean","INTERSECT",EDGE,{"disambiguationData":[OD(1.0)],"derivedFrom":[makeQuery(id+"F5.opExtrude","SWEPT_FACE",FACE,{"disambiguationData":[OSD([sQuery(id+"F4.wireOp",EDGE,"E30")])]}),makeQuery(id+"F8.opExtrude","SWEPT_FACE",FACE,{"disambiguationData":[OSD([sQuery(id+"F7.wireOp",EDGE,"E67")])]})]});
            var Q3;
            {var subQ0=sQuery(id+"F4.wireOp",EDGE,"E30");Q3=makeQuery(id+"F8.boolean.opBoolean","SPLIT",EDGE,{"disambiguationData":[TD([makeQuery(id+"F5.opExtrude","SWEPT_FACE",FACE,{"disambiguationData":[OSD([sQuery(id+"F4.wireOp",EDGE,"E35.filletArc")])]})])],"derivedFrom":makeQuery(id+"F5.opExtrude","CAP_EDGE",EDGE,{"disambiguationData":[OSD([subQ0])],"isStart":false})});}
            var Q4;
            {var subQ0=sQuery(id+"F0.wireOp",EDGE,"E25.7");var subQ1=sQuery(id+"F0.wireOp",EDGE,"E25.1");var subQ2=sQuery(id+"F0.wireOp",EDGE,"E25.6");var subQ3=sQuery(id+"F0.wireOp",EDGE,"E25.5");var subQ4=sQuery(id+"F0.wireOp",EDGE,"E25.4");var subQ5=sQuery(id+"F0.wireOp",EDGE,"E25.0");var subQ6=sQuery(id+"F0.wireOp",EDGE,"E25.2");var subQ7=sQuery(id+"F0.wireOp",EDGE,"E25.3");Q4=makeQuery(id+"F8.boolean.opBoolean","INTERSECT",EDGE,{"derivedFrom":[makeQuery(id+"F5.boolean.opBoolean","SPLIT",FACE,{"disambiguationData":[TD([makeQuery(id+"F2.opExtrude","SWEPT_FACE",FACE,{"disambiguationData":[OSD([subQ5])]})])],"derivedFrom":makeQuery(id+"F3.boolean.opBoolean","COPY",FACE,{"derivedFrom":makeQuery(id+"F3.opExtrude","CAP_FACE",FACE,{"disambiguationData":[OSD([subQ5,subQ1,subQ6,subQ7,subQ4,subQ3,subQ2,subQ0])],"isStart":false})})}),makeQuery(id+"F8.opExtrude","SWEPT_FACE",FACE,{"disambiguationData":[OSD([sQuery(id+"F7.wireOp",EDGE,"E67")])]})]});}
            var Q5;
            Q5=makeQuery(id+"F8.boolean.opBoolean","INTERSECT",EDGE,{"disambiguationData":[OD(0.0)],"derivedFrom":[makeQuery(id+"F5.opExtrude","SWEPT_FACE",FACE,{"disambiguationData":[OSD([sQuery(id+"F4.wireOp",EDGE,"E30")])]}),makeQuery(id+"F8.opExtrude","SWEPT_FACE",FACE,{"disambiguationData":[OSD([sQuery(id+"F7.wireOp",EDGE,"E67")])]})]});
            fillet(context, id + "F14", {"entities" : qUnion([Q0, Q1, Q2, Q3, Q4, Q5]), "radius" : 3 * mm, "tangentPropagation" : true, "allowEdgeOverflow" : false});
        }
        {
            var Q0;
            Q0=makeQuery(id+"F1.opExtrude","CAP_EDGE",EDGE,{"disambiguationData":[OSD([sQuery(id+"F0.wireOp",EDGE,"E1.bottom")])],"isStart":false});
            fillet(context, id + "F15", {"entities" : qUnion([Q0]), "radius" : 2 * mm, "tangentPropagation" : true, "allowEdgeOverflow" : false});
        }
        {
            var Q0;
            {var subQ0=sQuery(id+"F0.wireOp",EDGE,"E21.filletArc");var subQ1=sQuery(id+"F0.wireOp",EDGE,"E7");var subQ2=sQuery(id+"F0.wireOp",EDGE,"E6");var subQ3=sQuery(id+"F0.wireOp",EDGE,"E5");var subQ4=sQuery(id+"F0.wireOp",EDGE,"E4");var subQ5=sQuery(id+"F0.wireOp",EDGE,"E22.filletArc");var subQ6=sQuery(id+"F0.wireOp",EDGE,"E1.bottom");var subQ7=sQuery(id+"F0.wireOp",EDGE,"E1.right");var subQ8=sQuery(id+"F0.wireOp",EDGE,"E1.top");var subQ9=sQuery(id+"F0.wireOp",EDGE,"E1.left");var subQ10=sQuery(id+"F0.wireOp",EDGE,"E23.filletArc");var subQ11=sQuery(id+"F0.wireOp",EDGE,"E24.filletArc");Q0=makeQuery(id+"F2.boolean.opBoolean","SPLIT",FACE,{"disambiguationData":[TD([makeQuery(id+"F1.opExtrude","SWEPT_FACE",FACE,{"disambiguationData":[OSD([subQ6])]})])],"derivedFrom":makeQuery(id+"F1.opExtrude","CAP_FACE",FACE,{"disambiguationData":[OSD([subQ6,subQ8,subQ9,subQ7,subQ4,subQ3,subQ2,subQ1,subQ0,subQ5,subQ10,subQ11])],"isStart":true})});}
            var sketch = newSketch(context, id + "F16", { "sketchPlane" : qUnion([Q0])});
            skLineSegment(sketch, "E79.0.0", {"start": v(70, 90) * mm, "end": v(-70, 90) * mm});
            skArc(sketch, "E79.0.1", {"start": v(-70, 90) * mm, "mid": v(-77.07, 87.07) * mm, "end": v(-80, 80) * mm});
            skLineSegment(sketch, "E79.0.2", {"start": v(-80, 80) * mm, "end": v(-80, -80) * mm});
            skArc(sketch, "E79.0.3", {"start": v(-80, -80) * mm, "mid": v(-77.07, -87.07) * mm, "end": v(-70, -90) * mm});
            skLineSegment(sketch, "E79.0.4", {"start": v(-70, -90) * mm, "end": v(70, -90) * mm});
            skArc(sketch, "E79.0.5", {"start": v(70, -90) * mm, "mid": v(77.07, -87.07) * mm, "end": v(80, -80) * mm});
            skLineSegment(sketch, "E79.0.6", {"start": v(80, -80) * mm, "end": v(80, 80) * mm});
            skArc(sketch, "E79.0.7", {"start": v(80, 80) * mm, "mid": v(77.07, 87.07) * mm, "end": v(70, 90) * mm});
            skLineSegment(sketch, "E80", {"start": v(0, 120) * mm, "end": v(0, 90) * mm, "construction": true});
            skPoint(sketch, "E80.startSnap0", {"position": v(0, 90) * mm});
            skArc(sketch, "E81", {"start": v(15, 120) * mm, "mid": v(0, 135) * mm, "end": v(-15, 120) * mm});
            skCircle(sketch, "E82", {"center": v(0, 120) * mm, "radius": 6 * mm});
            skLineSegment(sketch, "E83", {"start": v(-15, 120) * mm, "end": v(-15, 108) * mm});
            skLineSegment(sketch, "E84", {"start": v(-15, 108) * mm, "end": v(-33, 90) * mm});
            skLineSegment(sketch, "E85", {"start": v(15, 120) * mm, "end": v(15, 108) * mm});
            skLineSegment(sketch, "E86", {"start": v(15, 108) * mm, "end": v(33, 90) * mm});
            skLineSegment(sketch, "E87", {"start": v(-80, 0) * mm, "end": v(80, 0) * mm, "construction": true});
            skLineSegment(sketch, "E88.MirrorCS", {"start": v(15, -108) * mm, "end": v(33, -90) * mm});
            skLineSegment(sketch, "E89.MirrorCS", {"start": v(15, -120) * mm, "end": v(15, -108) * mm});
            skLineSegment(sketch, "E90.MirrorCS", {"start": v(-15, -120) * mm, "end": v(-15, -108) * mm});
            skLineSegment(sketch, "E91.MirrorCS", {"start": v(0, -120) * mm, "end": v(0, -90) * mm, "construction": true});
            skArc(sketch, "E92.MirrorCS", {"start": v(15, -120) * mm, "mid": v(0, -135) * mm, "end": v(-15, -120) * mm});
            skCircle(sketch, "E93.MirrorC", {"center": v(0, -120) * mm, "radius": 6 * mm});
            skLineSegment(sketch, "E94.MirrorCS", {"start": v(-15, -108) * mm, "end": v(-33, -90) * mm});
            skPoint(sketch, "E95.MirrorP", {"position": v(0, -90) * mm});
            skSolve(sketch);
        }
        {
            var Q0;
            Q0=makeQuery(id+"F16.imprint","IMPRINT",FACE,{"disambiguationData":[TD([[makeQuery(id+"F16.imprint","IMPRINT",EDGE,{"derivedFrom":sQuery(id+"F16.wireOp",EDGE,"E81")}),1.0]])]});
            var Q1;
            {var subQ0=sQuery(id+"F16.wireOp",EDGE,"E88.MirrorCS");Q1=makeQuery(id+"F16.imprint","IMPRINT",FACE,{"disambiguationData":[TD([[makeQuery(id+"F16.imprint","IMPRINT",EDGE,{"derivedFrom":subQ0}),1.0]])]});}
            var Q2;
            {var subQ1=sQuery(id+"F16.wireOp",EDGE,"E79.0.1");Q2=makeQuery(id+"F16.imprint","IMPRINT",FACE,{"disambiguationData":[TD([[makeQuery(id+"F16.imprint","IMPRINT",EDGE,{"derivedFrom":subQ1}),1.0]])]});}
            var Q3;
            Q3=makeQuery(id+"F2.opExtrude","CAP_FACE",FACE,{"disambiguationData":[OSD([sQuery(id+"F0.wireOp",EDGE,"E12"),sQuery(id+"F0.wireOp",EDGE,"E13"),sQuery(id+"F0.wireOp",EDGE,"E14"),sQuery(id+"F0.wireOp",EDGE,"E15"),sQuery(id+"F0.wireOp",EDGE,"E17.filletArc"),sQuery(id+"F0.wireOp",EDGE,"E18.filletArc"),sQuery(id+"F0.wireOp",EDGE,"E19.filletArc"),sQuery(id+"F0.wireOp",EDGE,"E20.filletArc"),sQuery(id+"F0.wireOp",EDGE,"E25.0"),sQuery(id+"F0.wireOp",EDGE,"E25.1"),sQuery(id+"F0.wireOp",EDGE,"E25.2"),sQuery(id+"F0.wireOp",EDGE,"E25.3"),sQuery(id+"F0.wireOp",EDGE,"E25.4"),sQuery(id+"F0.wireOp",EDGE,"E25.5"),sQuery(id+"F0.wireOp",EDGE,"E25.6"),sQuery(id+"F0.wireOp",EDGE,"E25.7")])],"isStart":false});
            extrude(context, id + "F17", {"entities" : qUnion([Q0, Q1, Q2]), "endBound" : BoundingType.UP_TO_SURFACE, "depth" : 25 * mm, "endBoundEntityFace" : qUnion([Q3]), "offsetDistance" : 25 * mm});
        }
    });
